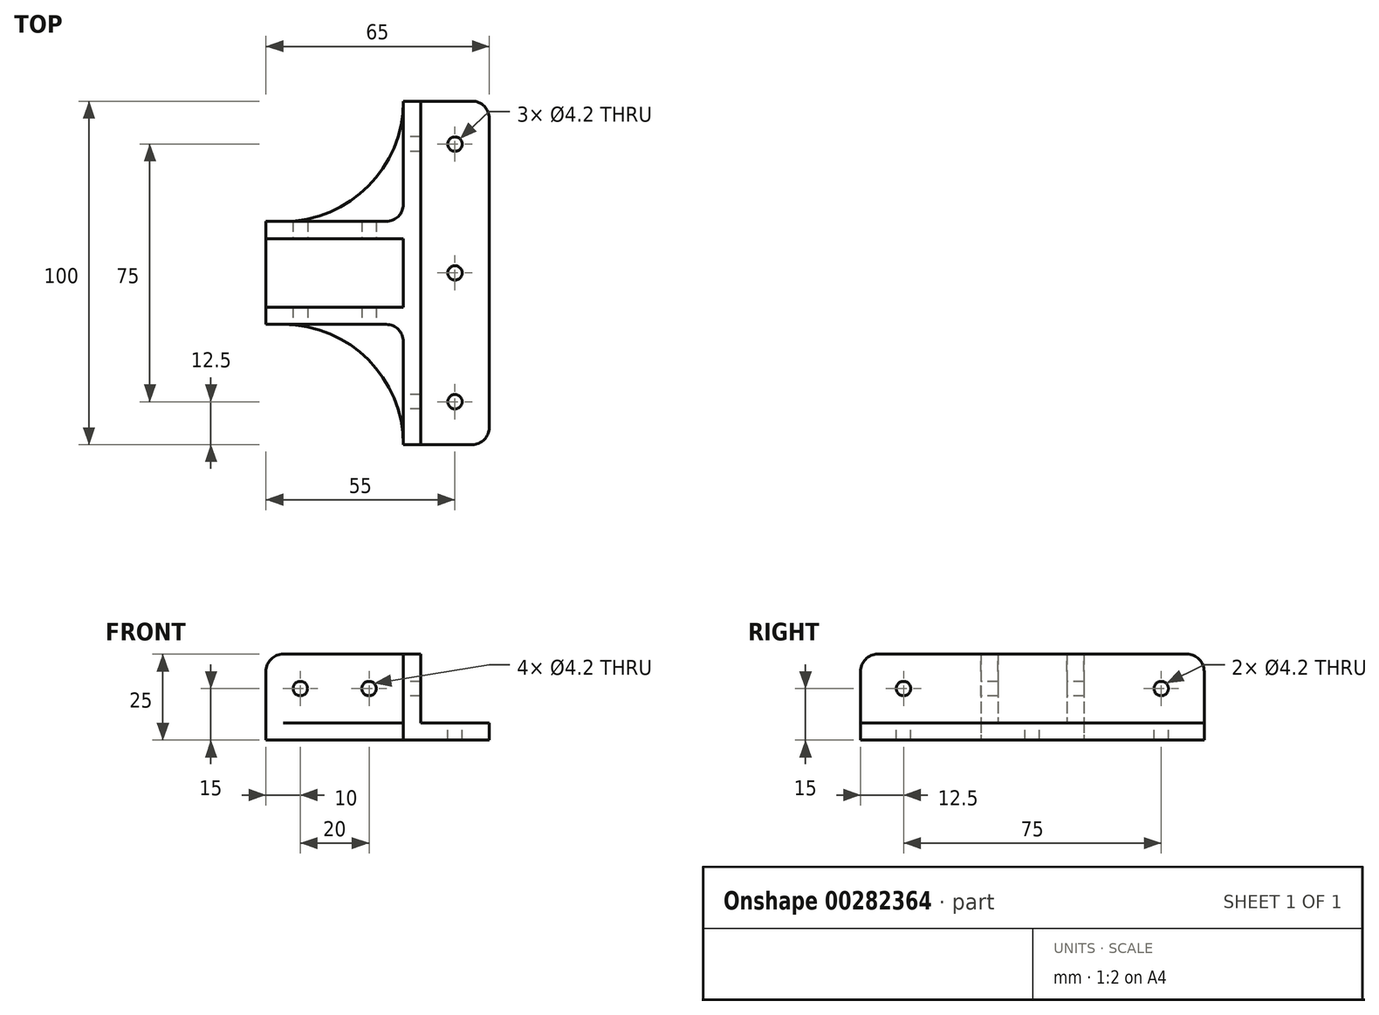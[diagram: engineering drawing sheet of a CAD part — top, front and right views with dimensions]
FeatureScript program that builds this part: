
annotation { "Feature Type Name" : "Feature", "Feature Type Description" : "" }
export const myFeature = defineFeature(function(context is Context, id is Id, definition is map)
    precondition{}
    {
        {
            var Q0;
            Q0=qCreatedBy(makeId("Top.planeOp"),FACE);
            var sketch = newSketch(context, id + "F0", { "sketchPlane" : qUnion([Q0])});
            skLineSegment(sketch, "E0", {"start": v(0, 0) * mm, "end": v(0, 50) * mm});
            skLineSegment(sketch, "E1", {"start": v(0, 50) * mm, "end": v(-25, 50) * mm});
            skLineSegment(sketch, "E2", {"start": v(0, 0) * mm, "end": v(-65, 0) * mm, "construction": true});
            skLineSegment(sketch, "E3", {"start": v(-65, 0) * mm, "end": v(-65, 15) * mm});
            skLineSegment(sketch, "E4.MirrorCS", {"start": v(-65, 0) * mm, "end": v(-65, -15) * mm});
            skLineSegment(sketch, "E5.MirrorCS", {"start": v(0, -50) * mm, "end": v(-25, -50) * mm});
            skLineSegment(sketch, "E6.MirrorCS", {"start": v(0, 0) * mm, "end": v(0, -50) * mm});
            skLineSegment(sketch, "E7", {"start": v(-65, 15) * mm, "end": v(-60, 15) * mm});
            skArc(sketch, "E8", {"start": v(-60, 15) * mm, "mid": v(-35.25, 25.25) * mm, "end": v(-25, 50) * mm});
            skLineSegment(sketch, "E9.MirrorCS", {"start": v(-65, -15) * mm, "end": v(-60, -15) * mm});
            skArc(sketch, "E10.MirrorCS", {"start": v(-60, -15) * mm, "mid": v(-35.25, -25.25) * mm, "end": v(-25, -50) * mm});
            skSolve(sketch);
        }
        {
            var Q0;
            Q0 = qSketchRegion(id + "F0", true);
            extrude(context, id + "F1", {"entities" : qUnion([Q0]), "depth" : 5 * mm});
        }
        {
            var Q0;
            Q0=makeQuery(id+"F1.opExtrude","CAP_FACE",FACE,{"disambiguationData":[OSD([sQuery(id+"F0.wireOp",EDGE,"E0"),sQuery(id+"F0.wireOp",EDGE,"E1"),sQuery(id+"F0.wireOp",EDGE,"E3"),sQuery(id+"F0.wireOp",EDGE,"i7gT3oJS-0e4q-uaKy-bP6a-Y87abFxrhB7R"),sQuery(id+"F0.wireOp",EDGE,"E4.MirrorCS"),sQuery(id+"F0.wireOp",EDGE,"4f72c253-e03a-442c-b8c5-d3529ee617b30.MirrorCS"),sQuery(id+"F0.wireOp",EDGE,"E5.MirrorCS"),sQuery(id+"F0.wireOp",EDGE,"E6.MirrorCS")])],"isStart":false});
            var sketch = newSketch(context, id + "F2", { "sketchPlane" : qUnion([Q0])});
            skLineSegment(sketch, "E11.bottom", {"start": v(-25, 50) * mm, "end": v(-20, 50) * mm});
            skLineSegment(sketch, "E11.top", {"start": v(-25, -50) * mm, "end": v(-20, -50) * mm});
            skLineSegment(sketch, "E11.left", {"start": v(-25, 50) * mm, "end": v(-25, 15) * mm});
            skLineSegment(sketch, "E11.right", {"start": v(-20, 50) * mm, "end": v(-20, -50) * mm});
            skLineSegment(sketch, "E12.bottom", {"start": v(-65, 15) * mm, "end": v(-25, 15) * mm});
            skLineSegment(sketch, "E12.top", {"start": v(-65, 10) * mm, "end": v(-25, 10) * mm});
            skLineSegment(sketch, "E12.left", {"start": v(-65, 15) * mm, "end": v(-65, 10) * mm});
            skLineSegment(sketch, "E13.bottom", {"start": v(-65, -15) * mm, "end": v(-25, -15) * mm});
            skLineSegment(sketch, "E13.top", {"start": v(-65, -10) * mm, "end": v(-25, -10) * mm});
            skLineSegment(sketch, "E13.left", {"start": v(-65, -15) * mm, "end": v(-65, -10) * mm});
            skLineSegment(sketch, "E14.trimOffspring", {"start": v(-25, 10) * mm, "end": v(-25, -10) * mm});
            skLineSegment(sketch, "E15.trimOffspring", {"start": v(-25, -15) * mm, "end": v(-25, -50) * mm});
            skSolve(sketch);
        }
        {
            var Q0;
            Q0 = qSketchRegion(id + "F2", true);
            extrude(context, id + "F3", {"entities" : qUnion([Q0]), "operationType" : NewBodyOperationType.ADD, "depth" : 20 * mm});
        }
        {
            var Q0;
            Q0=makeQuery(id+"F3.boolean.opBoolean","MERGE",FACE,{"derivedFrom":[makeQuery(id+"F1.opExtrude","SWEPT_FACE",FACE,{"disambiguationData":[OSD([sQuery(id+"F0.wireOp",EDGE,"E9.MirrorCS")])]}),makeQuery(id+"F3.opExtrude","SWEPT_FACE",FACE,{"disambiguationData":[OSD([sQuery(id+"F2.wireOp",EDGE,"E13.bottom")])]})]});
            var sketch = newSketch(context, id + "F4", { "sketchPlane" : qUnion([Q0])});
            skLineSegment(sketch, "E16", {"start": v(-65, 15) * mm, "end": v(-25, 15) * mm, "construction": true});
            skLineSegment(sketch, "E17", {"start": v(-45, 15) * mm, "end": v(-45, 25) * mm, "construction": true});
            skPoint(sketch, "E18", {"position": v(-55, 15) * mm});
            skPoint(sketch, "E19", {"position": v(-35, 15) * mm});
            skSolve(sketch);
        }
        {
            var Q0;
            Q0=makeQuery(id+"F3.opExtrude","SWEPT_FACE",FACE,{"disambiguationData":[OSD([sQuery(id+"F2.wireOp",EDGE,"E11.left")])]});
            var sketch = newSketch(context, id + "F5", { "sketchPlane" : qUnion([Q0])});
            skLineSegment(sketch, "E20", {"start": v(-50, 15) * mm, "end": v(50, 15) * mm, "construction": true});
            skPoint(sketch, "E20.endSnap0", {"position": v(-15, 15) * mm});
            skLineSegment(sketch, "E21", {"start": v(0, 15) * mm, "end": v(0, 25) * mm, "construction": true});
            skPoint(sketch, "E21.endSnap0", {"position": v(0, 15) * mm});
            skPoint(sketch, "E22", {"position": v(-37.5, 15) * mm});
            skPoint(sketch, "E23", {"position": v(37.5, 15) * mm});
            skSolve(sketch);
        }
        {
            var Q0;
            {var subQ0=sQuery(id+"F0.wireOp",EDGE,"E5.MirrorCS");var subQ1=sQuery(id+"F0.wireOp",EDGE,"E1");var subQ2=sQuery(id+"F0.wireOp",EDGE,"E6.MirrorCS");var subQ3=sQuery(id+"F0.wireOp",EDGE,"E0");Q0=makeQuery(id+"F3.boolean.opBoolean","SPLIT",FACE,{"disambiguationData":[TD([makeQuery(id+"F3.opExtrude","SWEPT_FACE",FACE,{"disambiguationData":[OSD([sQuery(id+"F2.wireOp",EDGE,"E11.right")])]})])],"derivedFrom":makeQuery(id+"F1.opExtrude","CAP_FACE",FACE,{"disambiguationData":[OSD([subQ3,subQ1,sQuery(id+"F0.wireOp",EDGE,"E3"),sQuery(id+"F0.wireOp",EDGE,"E4.MirrorCS"),subQ0,subQ2,sQuery(id+"F0.wireOp",EDGE,"E7"),sQuery(id+"F0.wireOp",EDGE,"E8"),sQuery(id+"F0.wireOp",EDGE,"E9.MirrorCS"),sQuery(id+"F0.wireOp",EDGE,"E10.MirrorCS")])],"isStart":false})});}
            var sketch = newSketch(context, id + "F6", { "sketchPlane" : qUnion([Q0])});
            skLineSegment(sketch, "E24", {"start": v(-10, 50) * mm, "end": v(-10, -50) * mm, "construction": true});
            skPoint(sketch, "E25", {"position": v(-10, 0) * mm});
            skPoint(sketch, "E26", {"position": v(-10, -37.5) * mm});
            skPoint(sketch, "E27", {"position": v(-10, 37.5) * mm});
            skSolve(sketch);
        }
        {
            var Q0;
            Q0=sQuery(id+"F6.wireOp",VERTEX,"E26");
            var Q1;
            Q1=sQuery(id+"F6.wireOp",VERTEX,"E25");
            var Q2;
            Q2=sQuery(id+"F5.wireOp",VERTEX,"E23");
            var Q3;
            Q3=sQuery(id+"F5.wireOp",VERTEX,"E22");
            var Q4;
            Q4=sQuery(id+"F6.wireOp",VERTEX,"E27");
            var Q5;
            Q5=sQuery(id+"F4.wireOp",VERTEX,"E18");
            var Q6;
            Q6=sQuery(id+"F4.wireOp",VERTEX,"E19");
            var Q7;
            Q7=makeQuery(id+"F1.opExtrude","SWEPT_BODY",BODY,{"disambiguationData":[OSD([sQuery(id+"F0.wireOp",EDGE,"E0"),sQuery(id+"F0.wireOp",EDGE,"E1"),sQuery(id+"F0.wireOp",EDGE,"E3"),sQuery(id+"F0.wireOp",EDGE,"E4.MirrorCS"),sQuery(id+"F0.wireOp",EDGE,"E5.MirrorCS"),sQuery(id+"F0.wireOp",EDGE,"E6.MirrorCS"),sQuery(id+"F0.wireOp",EDGE,"E7"),sQuery(id+"F0.wireOp",EDGE,"E8"),sQuery(id+"F0.wireOp",EDGE,"E9.MirrorCS"),sQuery(id+"F0.wireOp",EDGE,"E10.MirrorCS")])]});
            hole(context, id + "F7", {"style" : HoleStyle.SIMPLE, "endStyle" : HoleEndStyle.THROUGH, "standardTappedOrClearance" : lookupTablePath({ "standard" : "ISO", "size" : "4.2", "type" : "Drilled" }), "standardBlindInLast" : lookupTablePath({ "standard" : "ISO", "size" : "4.2", "type" : "Drilled" }), "holeDiameter" : 4.2 * mm, "tappedDepth" : 3 * mm, "tapClearance" : 3, "startFromSketch" : true, "locations" : qUnion([Q0, Q1, Q2, Q3, Q4, Q5, Q6]), "scope" : qUnion([Q7])});
        }
        {
            var Q0;
            Q0=makeQuery(id+"F3.opExtrude","CAP_EDGE",EDGE,{"disambiguationData":[OSD([sQuery(id+"F2.wireOp",EDGE,"E13.left")])],"isStart":false});
            var Q1;
            Q1=makeQuery(id+"F3.opExtrude","CAP_EDGE",EDGE,{"disambiguationData":[OSD([sQuery(id+"F2.wireOp",EDGE,"E12.left")])],"isStart":false});
            var Q2;
            Q2=makeQuery(id+"F3.opExtrude","CAP_EDGE",EDGE,{"disambiguationData":[OSD([sQuery(id+"F2.wireOp",EDGE,"E11.bottom")])],"isStart":false});
            var Q3;
            Q3=makeQuery(id+"F3.opExtrude","CAP_EDGE",EDGE,{"disambiguationData":[OSD([sQuery(id+"F2.wireOp",EDGE,"E11.top")])],"isStart":false});
            var Q4;
            Q4=makeQuery(id+"F1.opExtrude","SWEPT_EDGE",EDGE,{"disambiguationData":[OSD([sQuery(id+"F0.wireOp",EDGE,"E5.MirrorCS"),sQuery(id+"F0.wireOp",EDGE,"E6.MirrorCS")])]});
            var Q5;
            Q5=makeQuery(id+"F1.opExtrude","SWEPT_EDGE",EDGE,{"disambiguationData":[OSD([sQuery(id+"F0.wireOp",EDGE,"E0"),sQuery(id+"F0.wireOp",EDGE,"E1")])]});
            var Q6;
            Q6=makeQuery(id+"F3.opExtrude","SWEPT_EDGE",EDGE,{"disambiguationData":[OSD([sQuery(id+"F2.wireOp",EDGE,"E13.bottom"),sQuery(id+"F2.wireOp",EDGE,"E15.trimOffspring")])]});
            var Q7;
            Q7=makeQuery(id+"F3.opExtrude","SWEPT_EDGE",EDGE,{"disambiguationData":[OSD([sQuery(id+"F2.wireOp",EDGE,"E11.left"),sQuery(id+"F2.wireOp",EDGE,"E12.bottom")])]});
            fillet(context, id + "F8", {"entities" : qUnion([Q0, Q1, Q2, Q3, Q4, Q5, Q6, Q7]), "radius" : 5 * mm, "tangentPropagation" : true, "allowEdgeOverflow" : false});
        }
    });
